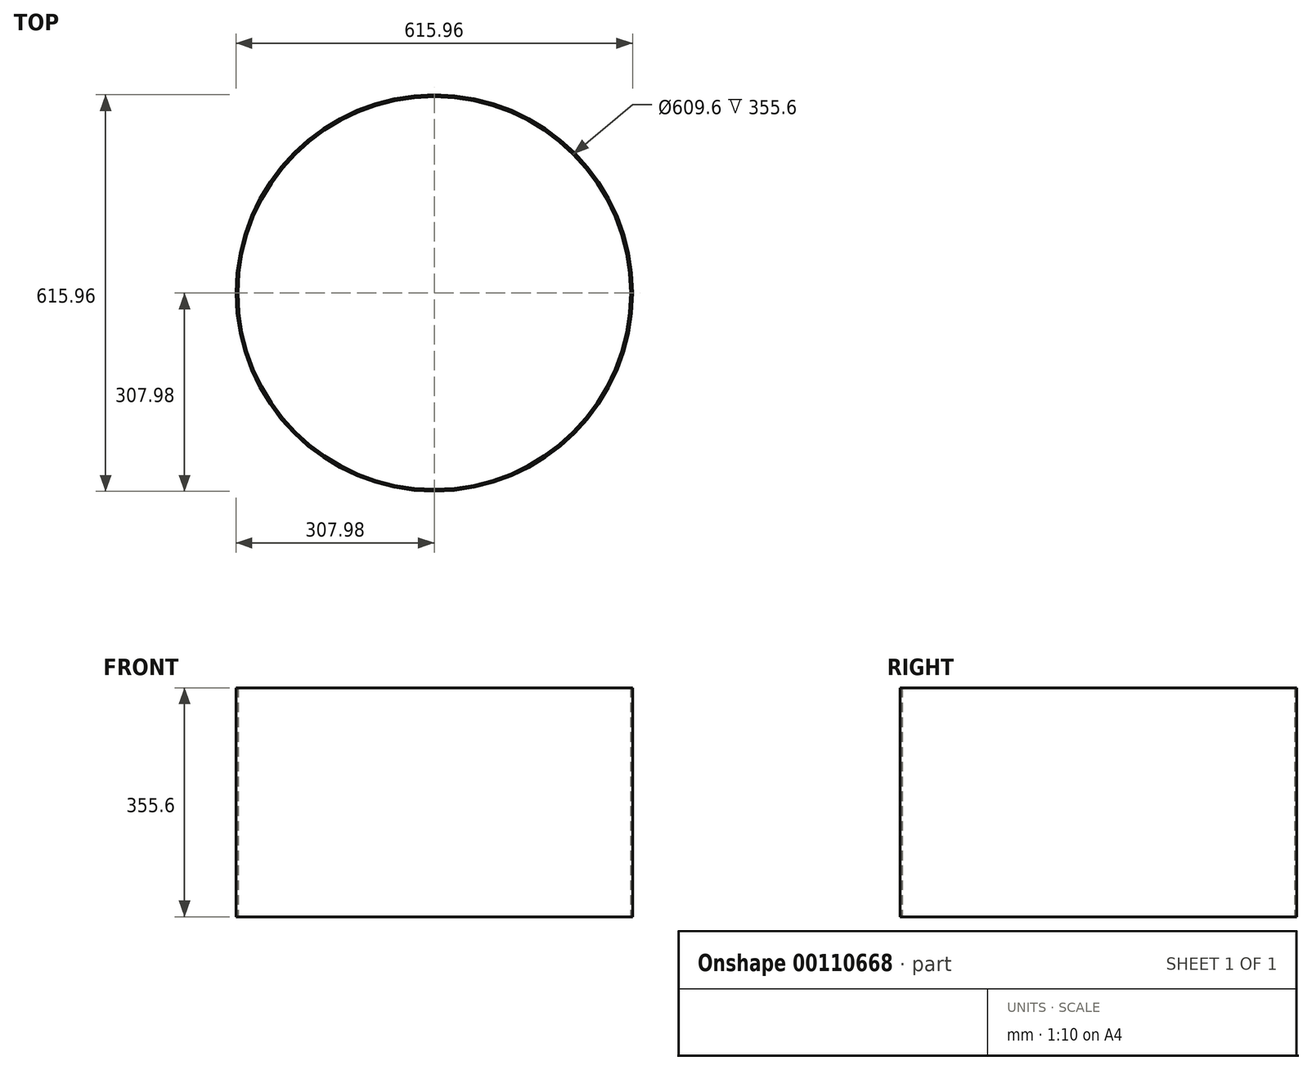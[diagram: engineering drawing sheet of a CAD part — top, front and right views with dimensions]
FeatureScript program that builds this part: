
annotation { "Feature Type Name" : "Feature", "Feature Type Description" : "" }
export const myFeature = defineFeature(function(context is Context, id is Id, definition is map)
    precondition{}
    {
        {
            var Q0;
            Q0=qCreatedBy(makeId("Top.planeOp"),FACE);
            var sketch = newSketch(context, id + "F0", { "sketchPlane" : qUnion([Q0])});
            skCircle(sketch, "E0", {"center": v(0, 0) * mm, "radius": 304.8 * mm});
            skCircle(sketch, "E1.0", {"center": v(0, 0) * mm, "radius": 307.98 * mm});
            skSolve(sketch);
        }
        {
            var Q0;
            Q0 = qSketchRegion(id + "F0", true);
            extrude(context, id + "F1", {"entities" : qUnion([Q0]), "depth" : 355.6 * mm});
        }
    });
